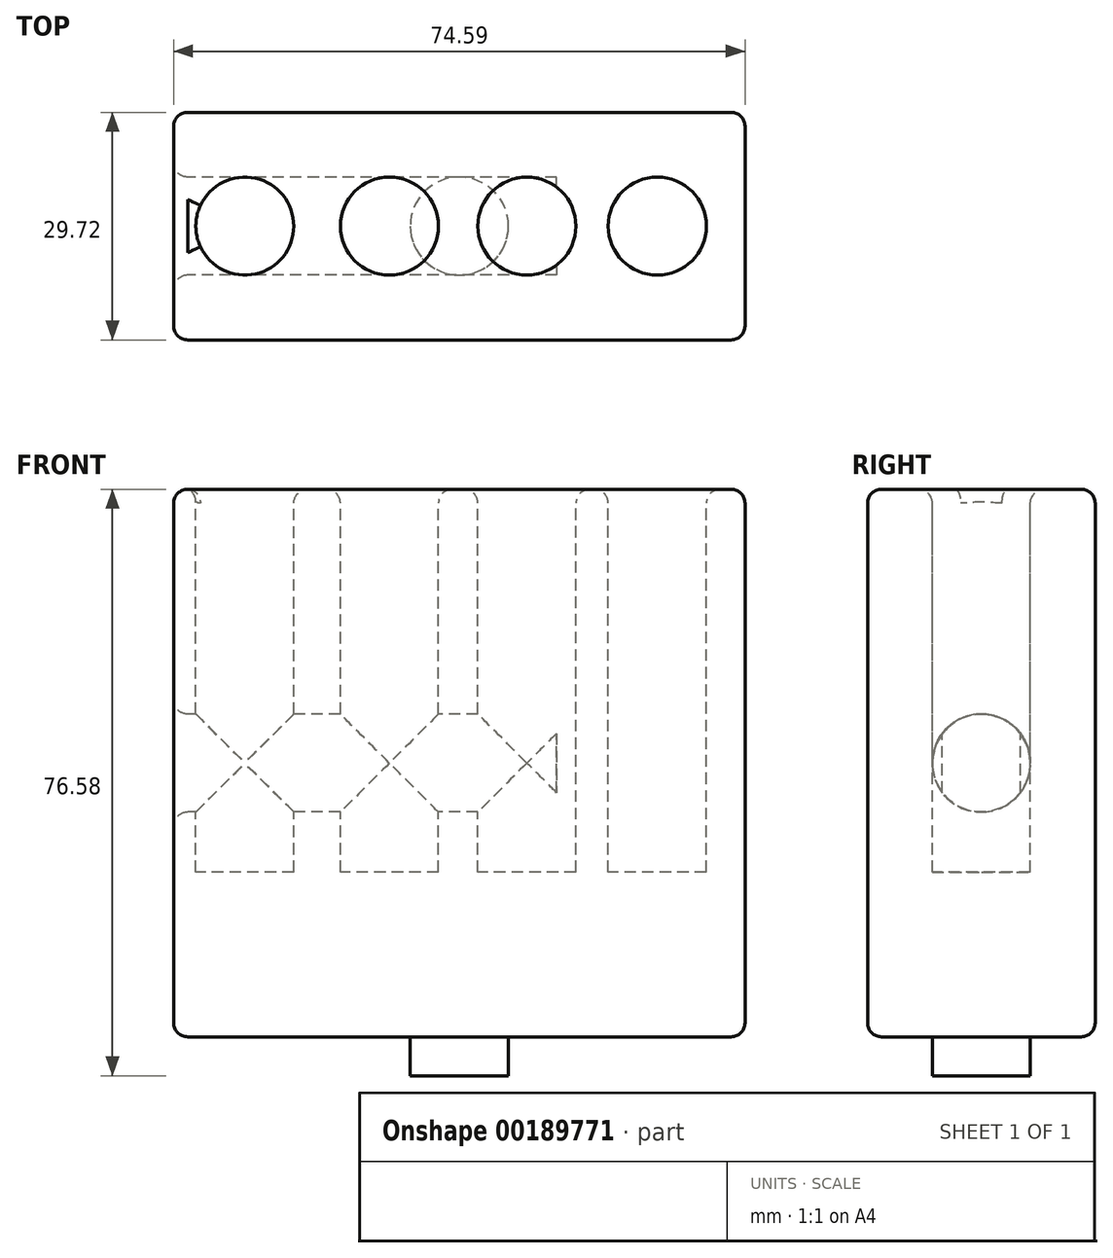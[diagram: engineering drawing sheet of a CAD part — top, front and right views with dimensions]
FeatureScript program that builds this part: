
annotation { "Feature Type Name" : "Feature", "Feature Type Description" : "" }
export const myFeature = defineFeature(function(context is Context, id is Id, definition is map)
    precondition{}
    {
        {
            var Q0;
            Q0=qCreatedBy(makeId("Front.planeOp"),FACE);
            var sketch = newSketch(context, id + "F0", { "sketchPlane" : qUnion([Q0])});
            skLineSegment(sketch, "E0.bottom", {"start": v(-31.88, 30.8) * mm, "end": v(42.71, 30.8) * mm});
            skLineSegment(sketch, "E0.top", {"start": v(-31.88, -40.7) * mm, "end": v(42.71, -40.7) * mm});
            skLineSegment(sketch, "E0.left", {"start": v(-31.88, 30.8) * mm, "end": v(-31.88, -40.7) * mm});
            skLineSegment(sketch, "E0.right", {"start": v(42.71, 30.8) * mm, "end": v(42.71, -40.7) * mm});
            skArc(sketch, "E1", {"start": v(42.71, 20.27) * mm, "mid": v(1.31, 19.8) * mm, "end": v(-31.88, -4.95) * mm});
            skArc(sketch, "E2", {"start": v(-31.88, -26.77) * mm, "mid": v(4.96, -35.7) * mm, "end": v(42.71, -32.34) * mm});
            skArc(sketch, "E3", {"start": v(-31.88, -4.95) * mm, "mid": v(5.95, 1.3) * mm, "end": v(42.71, 12.23) * mm});
            skArc(sketch, "E4", {"start": v(-31.88, 20.27) * mm, "mid": v(-18.63, 23.16) * mm, "end": v(-7.43, 30.8) * mm});
            skSolve(sketch);
        }
        {
            var Q0;
            {var subQ0=sQuery(id+"F0.wireOp",EDGE,"E1");Q0=makeQuery(id+"F0.imprint","IMPRINT",FACE,{"disambiguationData":[TD([[makeQuery(id+"F0.imprint","IMPRINT",EDGE,{"derivedFrom":subQ0}),-1.0]])]});}
            var Q1;
            {var subQ0=sQuery(id+"F0.wireOp",EDGE,"E1");Q1=makeQuery(id+"F0.imprint","IMPRINT",FACE,{"disambiguationData":[TD([[makeQuery(id+"F0.imprint","IMPRINT",EDGE,{"derivedFrom":subQ0}),1.0]])]});}
            var Q2;
            {var subQ2=sQuery(id+"F0.wireOp",EDGE,"E2");Q2=makeQuery(id+"F0.imprint","IMPRINT",FACE,{"disambiguationData":[TD([[makeQuery(id+"F0.imprint","IMPRINT",EDGE,{"derivedFrom":subQ2}),1.0]])]});}
            var Q3;
            {var subQ0=sQuery(id+"F0.wireOp",EDGE,"E0.top");Q3=makeQuery(id+"F0.imprint","IMPRINT",FACE,{"disambiguationData":[TD([[makeQuery(id+"F0.imprint","IMPRINT",EDGE,{"derivedFrom":subQ0}),1.0]])]});}
            var Q4;
            {var subQ3=sQuery(id+"F0.wireOp",EDGE,"E4");Q4=makeQuery(id+"F0.imprint","IMPRINT",FACE,{"disambiguationData":[TD([[makeQuery(id+"F0.imprint","IMPRINT",EDGE,{"derivedFrom":subQ3}),1.0]])]});}
            extrude(context, id + "F1", {"entities" : qUnion([Q0, Q1, Q2, Q3, Q4]), "depth" : 29.72 * mm});
        }
        {
            var Q0;
            Q0=makeQuery(id+"F1.opExtrude","CAP_FACE",FACE,{"disambiguationData":[OSD([sQuery(id+"F0.wireOp",EDGE,"E0.bottom"),sQuery(id+"F0.wireOp",EDGE,"E0.top"),sQuery(id+"F0.wireOp",EDGE,"E0.left"),sQuery(id+"F0.wireOp",EDGE,"E0.right")])],"isStart":false});
            fillet(context, id + "F2", {"entities" : qUnion([Q0]), "radius" : 1.83 * mm, "tangentPropagation" : true, "allowEdgeOverflow" : false});
        }
        {
            var Q0;
            Q0=makeQuery(id+"F1.opExtrude","CAP_FACE",FACE,{"disambiguationData":[OSD([sQuery(id+"F0.wireOp",EDGE,"E0.bottom"),sQuery(id+"F0.wireOp",EDGE,"E0.top"),sQuery(id+"F0.wireOp",EDGE,"E0.left"),sQuery(id+"F0.wireOp",EDGE,"E0.right")])],"isStart":true});
            fillet(context, id + "F3", {"entities" : qUnion([Q0]), "radius" : 1.83 * mm, "tangentPropagation" : true, "allowEdgeOverflow" : false});
        }
        {
            var Q0;
            Q0=makeQuery(id+"F1.opExtrude","SWEPT_FACE",FACE,{"disambiguationData":[OSD([sQuery(id+"F0.wireOp",EDGE,"E0.bottom")])]});
            var sketch = newSketch(context, id + "F4", { "sketchPlane" : qUnion([Q0])});
            skLineSegment(sketch, "E5", {"start": v(-31.88, -14.86) * mm, "end": v(42.71, -14.86) * mm, "construction": true});
            skLineSegment(sketch, "E6", {"start": v(-22.6, -27.89) * mm, "end": v(-22.6, -1.83) * mm, "construction": true});
            skLineSegment(sketch, "E7", {"start": v(-3.71, -27.89) * mm, "end": v(-3.71, -1.83) * mm, "construction": true});
            skLineSegment(sketch, "E8", {"start": v(14.24, -27.89) * mm, "end": v(14.24, -1.83) * mm, "construction": true});
            skLineSegment(sketch, "E9", {"start": v(31.26, -27.89) * mm, "end": v(31.26, 0) * mm, "construction": true});
            skCircle(sketch, "E10", {"center": v(-22.6, -14.86) * mm, "radius": 6.4 * mm});
            skCircle(sketch, "E11", {"center": v(-3.71, -14.86) * mm, "radius": 6.4 * mm});
            skCircle(sketch, "E12", {"center": v(14.24, -14.86) * mm, "radius": 6.4 * mm});
            skCircle(sketch, "E13", {"center": v(31.26, -14.86) * mm, "radius": 6.4 * mm});
            skPoint(sketch, "E13.centerSnap0", {"position": v(31.26, -13.94) * mm});
            skSolve(sketch);
        }
        {
            var Q0;
            Q0=makeQuery(id+"F4.imprint","IMPRINT",FACE,{"disambiguationData":[TD([[makeQuery(id+"F4.imprint","IMPRINT",EDGE,{"derivedFrom":sQuery(id+"F4.wireOp",EDGE,"E10")}),1.0]])]});
            var Q1;
            Q1=makeQuery(id+"F4.imprint","IMPRINT",FACE,{"disambiguationData":[TD([[makeQuery(id+"F4.imprint","IMPRINT",EDGE,{"derivedFrom":sQuery(id+"F4.wireOp",EDGE,"E11")}),1.0]])]});
            var Q2;
            Q2=makeQuery(id+"F4.imprint","IMPRINT",FACE,{"disambiguationData":[TD([[makeQuery(id+"F4.imprint","IMPRINT",EDGE,{"derivedFrom":sQuery(id+"F4.wireOp",EDGE,"E12")}),1.0]])]});
            var Q3;
            Q3=makeQuery(id+"F4.imprint","IMPRINT",FACE,{"disambiguationData":[TD([[makeQuery(id+"F4.imprint","IMPRINT",EDGE,{"derivedFrom":sQuery(id+"F4.wireOp",EDGE,"E13")}),1.0]])]});
            extrude(context, id + "F5", {"entities" : qUnion([Q0, Q1, Q2, Q3]), "operationType" : NewBodyOperationType.REMOVE, "oppositeDirection" : true, "depth" : 50 * mm});
        }
        {
            var Q0;
            Q0=makeQuery(id+"F1.opExtrude","SWEPT_FACE",FACE,{"disambiguationData":[OSD([sQuery(id+"F0.wireOp",EDGE,"E0.left")])]});
            var sketch = newSketch(context, id + "F6", { "sketchPlane" : qUnion([Q0])});
            skLineSegment(sketch, "E14", {"start": v(14.86, 30.8) * mm, "end": v(14.86, -40.7) * mm, "construction": true});
            skCircle(sketch, "E15", {"center": v(14.86, -4.95) * mm, "radius": 6.4 * mm});
            skSolve(sketch);
        }
        {
            var Q0;
            Q0=makeQuery(id+"F6.imprint","IMPRINT",FACE,{"disambiguationData":[TD([[makeQuery(id+"F6.imprint","IMPRINT",EDGE,{"derivedFrom":sQuery(id+"F6.wireOp",EDGE,"E15")}),1.0]])]});
            extrude(context, id + "F7", {"entities" : qUnion([Q0]), "operationType" : NewBodyOperationType.REMOVE, "oppositeDirection" : true, "depth" : 50 * mm});
        }
        {
            var Q0;
            Q0=makeQuery(id+"F1.opExtrude","SWEPT_FACE",FACE,{"disambiguationData":[OSD([sQuery(id+"F0.wireOp",EDGE,"E0.left")])]});
            fillet(context, id + "F8", {"entities" : qUnion([Q0]), "radius" : 1.83 * mm, "tangentPropagation" : true, "allowEdgeOverflow" : false});
        }
        {
            var Q0;
            Q0=makeQuery(id+"F1.opExtrude","SWEPT_FACE",FACE,{"disambiguationData":[OSD([sQuery(id+"F0.wireOp",EDGE,"E0.bottom")])]});
            fillet(context, id + "F9", {"entities" : qUnion([Q0]), "radius" : 1.83 * mm, "tangentPropagation" : true, "allowEdgeOverflow" : false});
        }
        {
            var Q0;
            Q0=makeQuery(id+"F1.opExtrude","SWEPT_FACE",FACE,{"disambiguationData":[OSD([sQuery(id+"F0.wireOp",EDGE,"E0.right")])]});
            fillet(context, id + "F10", {"entities" : qUnion([Q0]), "radius" : 1.83 * mm, "tangentPropagation" : true, "allowEdgeOverflow" : false});
        }
        {
            var Q0;
            Q0=makeQuery(id+"F1.opExtrude","SWEPT_FACE",FACE,{"disambiguationData":[OSD([sQuery(id+"F0.wireOp",EDGE,"E0.top")])]});
            var sketch = newSketch(context, id + "F11", { "sketchPlane" : qUnion([Q0])});
            skLineSegment(sketch, "E16", {"start": v(-30.05, 14.86) * mm, "end": v(40.88, 14.86) * mm, "construction": true});
            skCircle(sketch, "E17", {"center": v(5.42, 14.86) * mm, "radius": 6.4 * mm});
            skSolve(sketch);
        }
        {
            var Q0;
            Q0 = qSketchRegion(id + "F11", true);
            var Q1;
            Q1=sQuery(id+"F11.wireOp",EDGE,"E17");
            extrude(context, id + "F12", {"entities" : qUnion([Q0]), "operationType" : NewBodyOperationType.ADD, "surfaceEntities" : qUnion([Q1]), "depth" : 5.08 * mm});
        }
    });
